# Revit family: Gymnasium-Eqpt_Basketball_IPIbyBison_IP15WSF
name_source: partatom
category: Specialty Equipment
revit_build: Autodesk Revit 2018 (Build: 20170927_1515(x64)
units: mm (PartAtom-declared; Revit-internal decimal feet)

## family parameters
Always vertical = No
Cut with Voids When Loaded = No
Part Type = Normal
Room Calculation Point = No
Round Connector Dimension = Use Diameter
Shared = No
Work Plane-Based = Yes

## types (2) — shared parameters
Default Elevation = 0' - 0"
Manufacturer = IPI by Bison
Manufacturer Fax = 800-638-0698
Manufacturer Website = https://ipibybison.com
Product Data = http://www.arcat.com
Revision = R1_01-2018
Sales Information = https://ipibybison.com
URL = https://ipibybison.com
Unit Depth = 2' - 8"
Unit Width = 7' - 0"
wall distance text = 4 to 10 ft from Wall
zero-valued in all types: Expected Lifespan (Years), Maintenance Schedule (Months), Warranty Duration (Years)

## per-type parameters (varying)
| type | Description | Fold Left | Fold Right | Model |
| Wall Mounted Fold Right | IPI by Bison Wall Mounted Right Folding Basketball Backboard - IP15WSF as Specified | No | Yes | IP15WSF Right |
| Wall Mounted Fold Left | IPI by Bison Wall Mounted Left Folding Basketball Backboard - IP15WSF as Specified | Yes | No | IP15WSF Left |

## geometry (parser evidence)
native form markers: Sweep x6
no freeform markers — native parametric forms only
